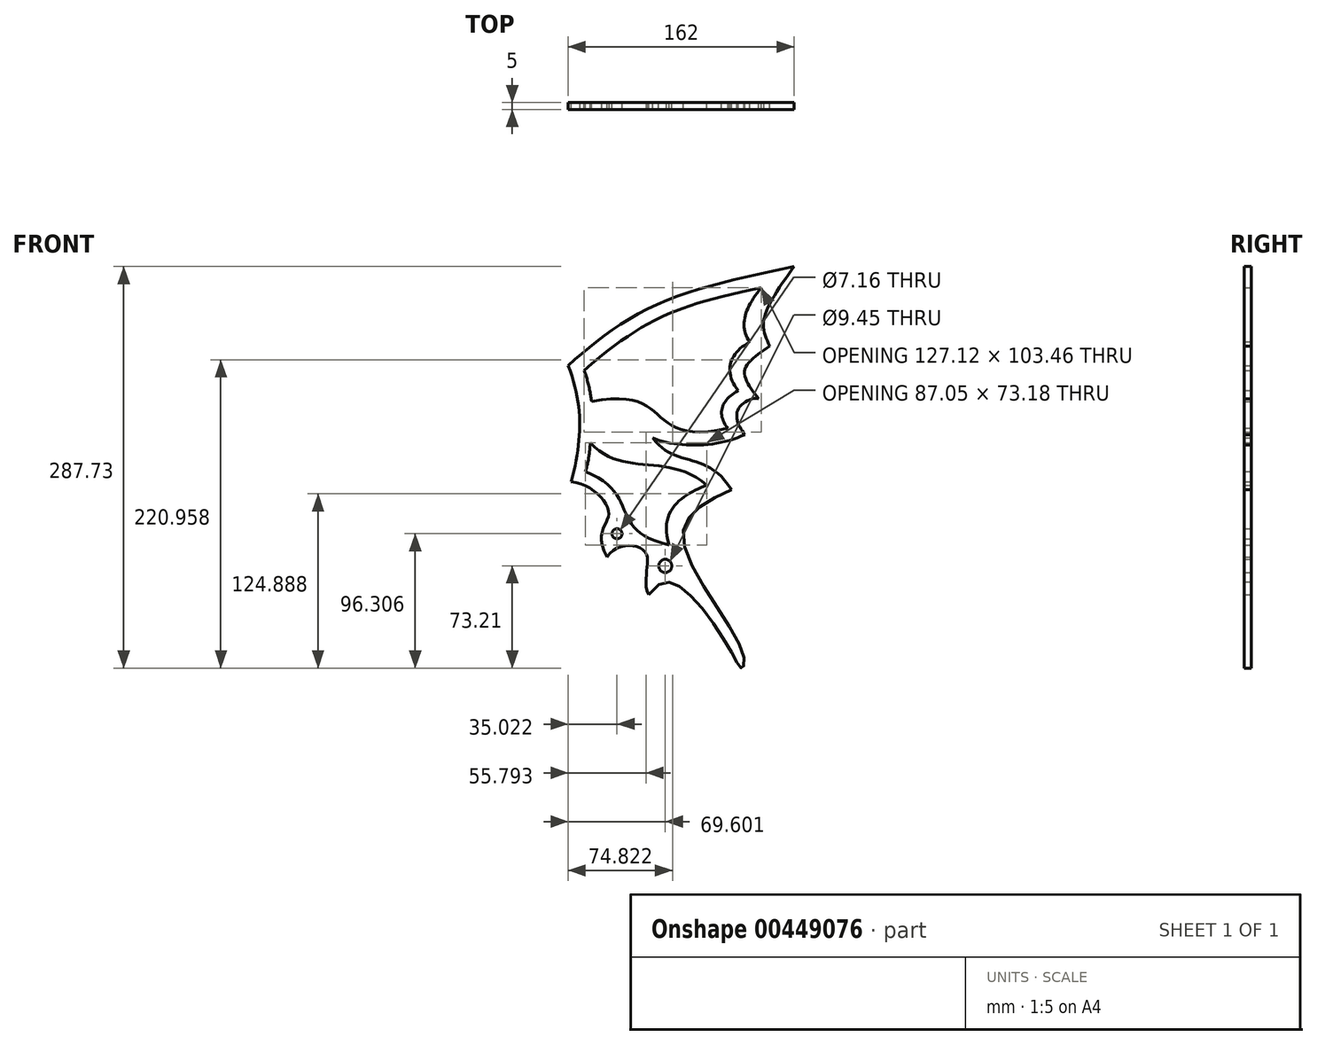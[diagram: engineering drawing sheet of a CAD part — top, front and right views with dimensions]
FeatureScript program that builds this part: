
annotation { "Feature Type Name" : "Feature", "Feature Type Description" : "" }
export const myFeature = defineFeature(function(context is Context, id is Id, definition is map)
    precondition{}
    {
        {
            var Q0;
            Q0=qCreatedBy(makeId("Front.planeOp"),FACE);
            var sketch = newSketch(context, id + "F0", { "sketchPlane" : qUnion([Q0])});
            skFitSpline(sketch, "E0", {"points": [v(2.74, 35.28) * mm, v(22.61, 49.27) * mm, v(56.74, 58.95) * mm], "startDerivative": vector(36.92, 33.2) * mm, "endDerivative": vector(67.1, 13.86) * mm});
            skFitSpline(sketch, "E1", {"points": [v(56.74, 58.95) * mm, v(49.44, 45.99) * mm, v(50.9, 39.97) * mm], "startDerivative": vector(-16.8, -23.14) * mm, "endDerivative": vector(6.8, -14.18) * mm});
            skFitSpline(sketch, "E2", {"points": [v(50.9, 39.97) * mm, v(44.88, 33.94) * mm, v(48.22, 27.4) * mm], "startDerivative": vector(-15.94, -10.93) * mm, "endDerivative": vector(9.86, -13.57) * mm});
            skFitSpline(sketch, "E3", {"points": [v(48.22, 27.4) * mm, v(43.17, 24.37) * mm, v(44.93, 18.81) * mm], "startDerivative": vector(-11.87, 2.06) * mm, "endDerivative": vector(7.26, -9.48) * mm});
            skFitSpline(sketch, "E4", {"points": [v(44.93, 18.81) * mm, v(22.96, 18.02) * mm], "startDerivative": vector(-19.82, -9.72) * mm, "endDerivative": vector(-16.72, 7.1) * mm});
            skFitSpline(sketch, "E5", {"points": [v(22.96, 18.02) * mm, v(41.79, 5.66) * mm], "startDerivative": vector(15.97, -22.46) * mm, "endDerivative": vector(18.76, -29.35) * mm});
            skFitSpline(sketch, "E6", {"points": [v(41.79, 5.66) * mm, v(30.15, -5.56) * mm, v(44.3, -32.88) * mm, v(44.25, -36.96) * mm, v(41.52, -32.8) * mm, v(29.36, -17.47) * mm, v(21.98, -19.4) * mm], "startDerivative": vector(-96.14, -44.69) * mm, "endDerivative": vector(-58.8, -77.1) * mm});
            skFitSpline(sketch, "E7", {"points": [v(21.98, -19.4) * mm, v(21.13, -9.29) * mm, v(12.06, -10.46) * mm], "startDerivative": vector(-10.44, 21.06) * mm, "endDerivative": vector(-13.25, -22.74) * mm});
            skFitSpline(sketch, "E8", {"points": [v(12.06, -10.46) * mm, v(12.42, 0) * mm, v(3.5, 7.54) * mm], "startDerivative": vector(-20.8, 37.3) * mm, "endDerivative": vector(-26.74, 2.15) * mm});
            skFitSpline(sketch, "E9", {"points": [v(3.5, 7.54) * mm, v(2.74, 35.28) * mm], "startDerivative": vector(7.4, 30.33) * mm, "endDerivative": vector(-11.59, 29.77) * mm});
            skPoint(sketch, "E10", {"position": v(0, 26.12) * mm});
            skFitSpline(sketch, "E11", {"points": [v(6.5, 34.15) * mm, v(48.87, 53.93) * mm], "startDerivative": vector(44.14, 38.21) * mm, "endDerivative": vector(58.85, 12.42) * mm});
            skFitSpline(sketch, "E12", {"points": [v(48.87, 53.93) * mm, v(46.14, 40.98) * mm], "startDerivative": vector(-12.23, -15.28) * mm, "endDerivative": vector(8.02, -11.27) * mm});
            skFitSpline(sketch, "E13", {"points": [v(46.14, 40.98) * mm, v(43.35, 29.32) * mm], "startDerivative": vector(-15.24, -8.6) * mm, "endDerivative": vector(10.56, -13.76) * mm});
            skFitSpline(sketch, "E14", {"points": [v(6.5, 34.15) * mm, v(8.36, 26.68) * mm], "startDerivative": vector(2.57, -5.54) * mm, "endDerivative": vector(0.78, -6.29) * mm});
            skFitSpline(sketch, "E15", {"points": [v(8.07, 16.86) * mm, v(35.85, 6.76) * mm], "startDerivative": vector(23.87, -25.9) * mm, "endDerivative": vector(29.39, -24.7) * mm});
            skFitSpline(sketch, "E16", {"points": [v(35.85, 6.76) * mm, v(26.89, -7.53) * mm], "startDerivative": vector(-15.22, -6.25) * mm, "endDerivative": vector(8.74, -26.4) * mm});
            skFitSpline(sketch, "E17", {"points": [v(26.89, -7.53) * mm, v(6.83, 9.98) * mm], "startDerivative": vector(-45.06, 9.73) * mm, "endDerivative": vector(-40.55, 15.82) * mm});
            skFitSpline(sketch, "E18", {"points": [v(6.83, 9.98) * mm, v(8.07, 16.86) * mm], "startDerivative": vector(2.61, 7.21) * mm, "endDerivative": vector(0.88, 6.72) * mm});
            skCircle(sketch, "E19", {"center": v(25.94, -12.56) * mm, "radius": 1.57 * mm});
            skCircle(sketch, "E20", {"center": v(14.41, -4.86) * mm, "radius": 1.2 * mm});
            skFitSpline(sketch, "E21", {"points": [v(43.35, 29.32) * mm, v(40.9, 20.38) * mm], "startDerivative": vector(-11.68, -6.22) * mm, "endDerivative": vector(8.6, -10.05) * mm});
            skFitSpline(sketch, "E22", {"points": [v(40.9, 20.38) * mm, v(8.36, 26.68) * mm], "startDerivative": vector(-61.46, -14.36) * mm, "endDerivative": vector(-60.19, -12.4) * mm});
            skSolve(sketch);
        }
        {
            var Q0;
            Q0=makeQuery(id+"F0.imprint","IMPRINT",FACE,{"disambiguationData":[TD([[makeQuery(id+"F0.imprint","IMPRINT",EDGE,{"derivedFrom":sQuery(id+"F0.wireOp",EDGE,"E0")}),-1.0]])]});
            extrude(context, id + "F1", {"entities" : qUnion([Q0]), "depth" : (5 / 3) * mm});
        }
        {
            var Q0;
            Q0=makeQuery(id+"F1.opExtrude","SWEPT_BODY",BODY,{"disambiguationData":[OSD([sQuery(id+"F0.wireOp",EDGE,"E0"),sQuery(id+"F0.wireOp",EDGE,"E1"),sQuery(id+"F0.wireOp",EDGE,"E2"),sQuery(id+"F0.wireOp",EDGE,"E3"),sQuery(id+"F0.wireOp",EDGE,"E4"),sQuery(id+"F0.wireOp",EDGE,"E5"),sQuery(id+"F0.wireOp",EDGE,"E6"),sQuery(id+"F0.wireOp",EDGE,"E7"),sQuery(id+"F0.wireOp",EDGE,"E8"),sQuery(id+"F0.wireOp",EDGE,"E9")])]});
            var Q1;
            Q1=qCreatedBy(makeId("Origin.pointOp"),VERTEX);
            transform(context, id + "F2", {"entities" : qUnion([Q0]), "transformType" : TransformType.SCALE_UNIFORMLY, "scale" : 3, "scalePoint" : qUnion([Q1]), "makeCopy" : false});
        }
    });
